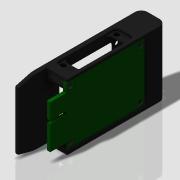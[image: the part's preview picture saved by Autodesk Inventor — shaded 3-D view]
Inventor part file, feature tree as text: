
AUTODESK INVENTOR PART (.ipt)
format: ipt  version: 2013 (Build 170138000, 138)  size: 478,720 bytes
history: native  units: in
note: dims shown in document units (in); Inventor stores cm internally (conversion verified against a paired STEP export)
features: extrude x13, sketch x13, thread x4, fillet x3
ambient origin geometry x8: Origin, YZ Plane, XZ Plane, XY Plane, X Axis, Y Axis, Z Axis, Center Point
bodies: Solid1 (feature_tree)
feature tree (33):
  extrude  "Extrusion1"  Depth=0.0984in
  extrude  "Extrusion2"  Depth=0.063in TaperAngle=0.0deg
  extrude  "Extrusion3"  Depth=0.07in
  extrude  "Extrusion4"  Depth=0.1535in
  fillet  "Fillet1"  Radius=0.311in
  fillet  "Fillet2"  Radius=0.0787in
  thread  "Thread1"  [1 undecoded]
  thread  "Thread2"  [1 undecoded]
  thread  "Thread3"  [1 undecoded]
  thread  "Thread4"  [1 undecoded]
  extrude  "Extrusion6"  Depth=0.1575in
  extrude  "Extrusion7"  Depth=0.315in TaperAngle=0.0deg
  extrude  "Extrusion8"  TaperAngle=105.0deg  [1 undecoded]
  fillet  "Fillet4"  Radius=0.0787in
  extrude  "Extrusion5"  Depth=0.0787in
  extrude  "Extrusion9"  Depth=0.0787in TaperAngle=0.0deg
  extrude  "Extrusion10"  Depth=0.0591in
  extrude  "Extrusion11"  Depth=0.3937in TaperAngle=0.0deg
  extrude  "Extrusion12"  Depth=0.0394in
  extrude  "Extrusion13"  Depth=0.3937in TaperAngle=0.0deg
  sketch  "Sketch1"  dims[d0=1.1in d5=0.0984in]
  sketch  "Sketch2"  dims[d6=0.0787in d12=0.063in d13=0.0in]
  sketch  "Sketch3"  dims[d21=0.459in d23=0.07in]
  sketch  "Sketch4"  dims[d27=1.5in d29=0.1535in d30=0.311in d31=0.0787in d32=0.0984in d33=0.0787in d34=0.0787in d35=0.1575in]
  sketch  "Sketch5"  dims[d38=0.1575in d39=0.1575in]
  sketch  "Sketch6"  dims[d40=0.1575in d41=0.315in d42=0.0in]
  sketch  "Sketch7"  dims[d43=105.0deg d44=105.0deg d45=0.0787in]
  sketch  "Sketch8"  dims[d46=0.0787in d47=0.0787in]
  sketch  "Sketch9"  dims[d48=0.2362in d49=0.0787in d50=0.0in]
  sketch  "Sketch10"  dims[d51=0.0591in d52=0.0591in]
  sketch  "Sketch11"  dims[d53=0.0591in d54=0.3937in d55=0.0in]
  sketch  "Sketch12"  dims[d56=0.0394in d57=0.0394in]
  sketch  "Sketch13"  dims[d58=0.3937in d59=0.0in d60=0.3937in d61=0.0in d62=0.3937in d63=0.0in d64=0.3937in d65=0.0in d69=0.0787in d70=0.0787in d71=0.2362in d72=0.0394in d73=0.0in d79=0.0039in d80=0.0in d83=0.0787in d84=0.1969in d86=0.0394in d87=0.0in d88=0.0591in d89=0.0787in d90=0.315in d91=0.0in d92=0.1181in d93=0.0591in d94=0.1575in d95=0.0787in d96=0.1575in d97=0.1575in d98=0.0984in d99=0.0787in d100=0.0984in d102=0.0394in d103=0.0in d104=0.0787in d105=0.0787in d106=0.0787in d107=0.0591in d108=0.0591in d109=0.0591in d110=0.0591in d111=0.0787in d112=0.1575in d113=0.1575in d114=0.0748in d115=0.0in d116=0.0984in d117=0.0787in d118=0.0787in d119=0.0984in d120=0.0787in d121=0.1575in d122=0.5512in d123=0.0591in d124=0.0787in d125=0.5512in d126=0.0394in d127=0.0in d128=0.0787in d129=0.1575in d130=0.1575in d131=0.0984in d133=0.0394in d134=0.0in d135=0.0984in d137=0.5906in d138=0.0787in d139=0.1575in d140=0.1575in d141=0.0984in d142=0.0984in d145=0.0394in d146=0.0in d147=0.0787in d148=0.2992in d149=0.0787in d150=0.0787in d151=1.3583in d152=1.0433in d153=1.3583in d154=0.8661in d155=0.8661in]
note: 5 required parameter values undecoded (feature->parameter linkage not recoverable at this tier; creation-order binding heuristic only, values carry confidence <= 0.55)
